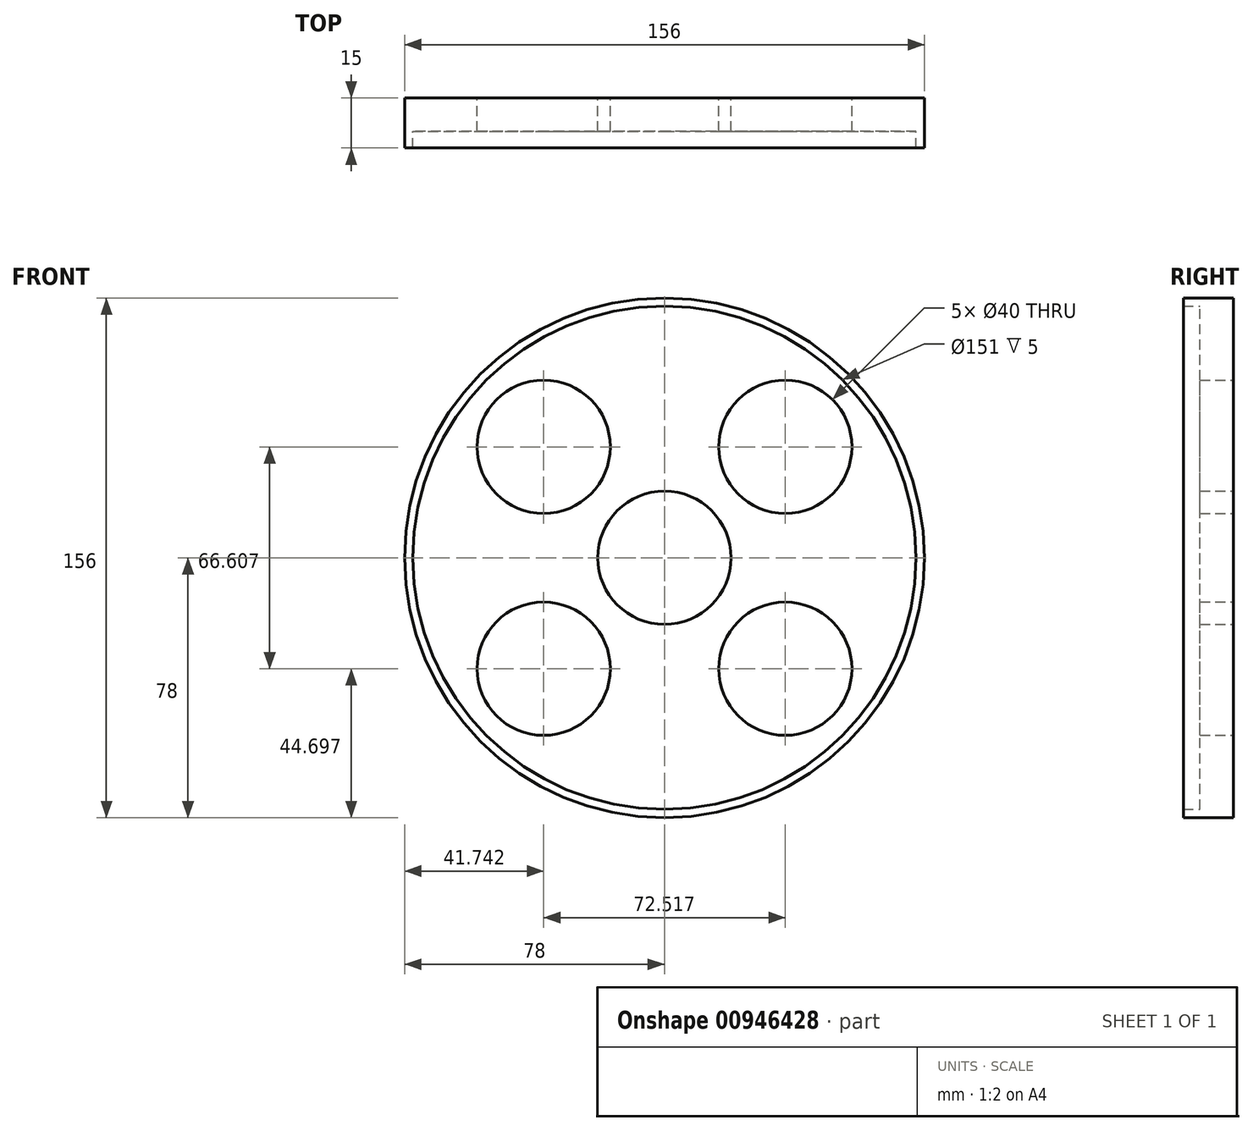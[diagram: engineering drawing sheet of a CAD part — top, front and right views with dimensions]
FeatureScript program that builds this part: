
annotation { "Feature Type Name" : "Feature", "Feature Type Description" : "" }
export const myFeature = defineFeature(function(context is Context, id is Id, definition is map)
    precondition{}
    {
        {
            var Q0;
            Q0=qCreatedBy(makeId("Front.planeOp"),FACE);
            var sketch = newSketch(context, id + "F0", { "sketchPlane" : qUnion([Q0])});
            skCircle(sketch, "E0", {"center": v(0, 0) * mm, "radius": 78 * mm});
            skCircle(sketch, "E1", {"center": v(0, 0) * mm, "radius": 20 * mm});
            skCircle(sketch, "E2", {"center": v(-36.26, 33.3) * mm, "radius": 20 * mm});
            skCircle(sketch, "E3", {"center": v(36.26, 33.3) * mm, "radius": 20 * mm});
            skCircle(sketch, "E4", {"center": v(36.26, -33.3) * mm, "radius": 20 * mm});
            skCircle(sketch, "E5", {"center": v(-36.26, -33.3) * mm, "radius": 20 * mm});
            skCircle(sketch, "E6", {"center": v(0, 0) * mm, "radius": 75.5 * mm});
            skSolve(sketch);
        }
        {
            var Q0;
            Q0=makeQuery(id+"F0.imprint","IMPRINT",FACE,{"disambiguationData":[TD([[makeQuery(id+"F0.imprint","IMPRINT",EDGE,{"derivedFrom":sQuery(id+"F0.wireOp",EDGE,"E1")}),-1.0]])]});
            extrude(context, id + "F1", {"entities" : qUnion([Q0]), "depth" : 10 * mm, "offsetDistance" : 25.4 * mm});
        }
        {
            var Q0;
            Q0=makeQuery(id+"F0.imprint","IMPRINT",FACE,{"disambiguationData":[TD([[makeQuery(id+"F0.imprint","IMPRINT",EDGE,{"derivedFrom":sQuery(id+"F0.wireOp",EDGE,"E0")}),1.0]])]});
            extrude(context, id + "F2", {"entities" : qUnion([Q0]), "operationType" : NewBodyOperationType.ADD, "depth" : 15 * mm, "offsetDistance" : 25.4 * mm});
        }
    });
